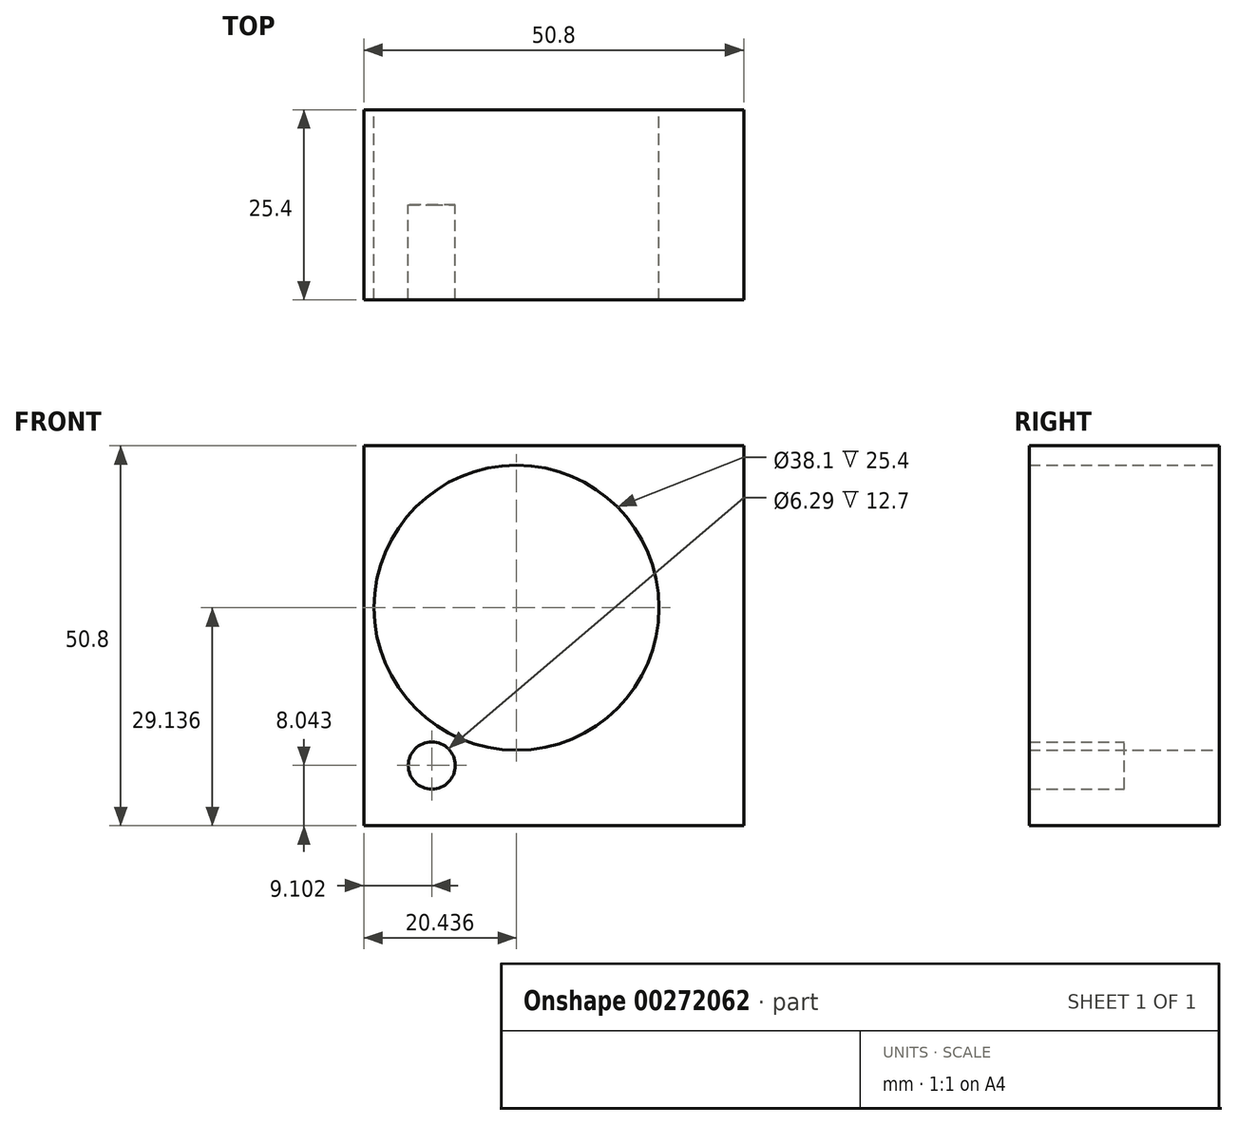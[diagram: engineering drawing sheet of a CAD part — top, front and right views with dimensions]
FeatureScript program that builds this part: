
annotation { "Feature Type Name" : "Feature", "Feature Type Description" : "" }
export const myFeature = defineFeature(function(context is Context, id is Id, definition is map)
    precondition{}
    {
        {
            var Q0;
            Q0=qCreatedBy(makeId("Front.planeOp"),FACE);
            var sketch = newSketch(context, id + "F0", { "sketchPlane" : qUnion([Q0])});
            skLineSegment(sketch, "E0.bottom", {"start": v(0, 0) * mm, "end": v(50.8, 0) * mm});
            skLineSegment(sketch, "E0.top", {"start": v(0, 50.8) * mm, "end": v(50.8, 50.8) * mm});
            skLineSegment(sketch, "E0.left", {"start": v(0, 0) * mm, "end": v(0, 50.8) * mm});
            skLineSegment(sketch, "E0.right", {"start": v(50.8, 0) * mm, "end": v(50.8, 50.8) * mm});
            skCircle(sketch, "E1", {"center": v(20.44, 29.14) * mm, "radius": 19.05 * mm});
            skCircle(sketch, "E2", {"center": v(9.1, 8.04) * mm, "radius": 3.15 * mm});
            skSolve(sketch);
        }
        {
            var Q0;
            Q0=makeQuery(id+"F0.imprint","IMPRINT",FACE,{"disambiguationData":[TD([[makeQuery(id+"F0.imprint","IMPRINT",EDGE,{"derivedFrom":sQuery(id+"F0.wireOp",EDGE,"E0.bottom")}),1.0]])]});
            extrude(context, id + "F1", {"entities" : qUnion([Q0]), "depth" : 25.4 * mm});
        }
        {
            var Q0;
            Q0=makeQuery(id+"F0.imprint","IMPRINT",FACE,{"disambiguationData":[TD([[makeQuery(id+"F0.imprint","IMPRINT",EDGE,{"derivedFrom":sQuery(id+"F0.wireOp",EDGE,"E2")}),1.0]])]});
            var Q1;
            Q1=sQuery(id+"F0.wireOp",EDGE,"E2");
            extrude(context, id + "F2", {"entities" : qUnion([Q0]), "operationType" : NewBodyOperationType.ADD, "surfaceEntities" : qUnion([Q1]), "depth" : 12.7 * mm});
        }
    });
